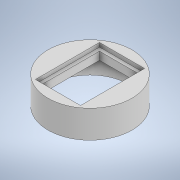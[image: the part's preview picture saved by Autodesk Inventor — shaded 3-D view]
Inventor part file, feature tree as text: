
AUTODESK INVENTOR PART (.ipt)
format: ipt  version: 2020 (Build 240168000, 168)  size: 125,440 bytes
history: native  units: in
note: dims shown in document units (in); Inventor stores cm internally (conversion verified against a paired STEP export)
features: extrude x4, sketch x4
ambient origin geometry x8: Origin, YZ Plane, XZ Plane, XY Plane, X Axis, Y Axis, Z Axis, Center Point
bodies: Solid1 (feature_tree)
feature tree (8):
  extrude  "Extrusion1"  Depth=2.4in
  extrude  "Extrusion2"  Depth=0.375in TaperAngle=0.0deg
  extrude  "Extrusion3"  Depth=2.025in
  extrude  "Extrusion4"  Depth=1.2in
  sketch  "Sketch1"  dims[d0=2.65in d1=2.4in]
  sketch  "Sketch2"  dims[d2=0.5in d3=0.0in d4=0.375in d5=0.0in]
  sketch  "Sketch3"  dims[d6=1.425in d7=2.025in]
  sketch  "Sketch4"  dims[d8=0.125in d9=0.0in d10=1.2in d11=1.8in d12=0.0in d13=0.0in]
